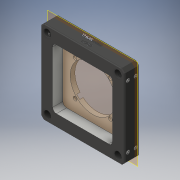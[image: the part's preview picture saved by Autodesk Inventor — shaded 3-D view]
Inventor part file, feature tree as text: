
AUTODESK INVENTOR PART (.ipt)
format: ipt  version: 2016 (Build 200138000, 138)  size: 1,070,592 bytes
history: native  units: in
note: dims shown in document units (in); Inventor stores cm internally (conversion verified against a paired STEP export)
features: other x9, sketch x4, projected_geometry x4, extrude x3, plane x1, hole x1, pattern_circular x1
ambient origin geometry x8: Origin, YZ Plane, XZ Plane, XY Plane, X Axis, Y Axis, Z Axis, Center Point
bodies: Solid1 (feature_tree), Solid2 (feature_tree), Solid3 (feature_tree), Solid4 (feature_tree), Solid5 (feature_tree), Solid6 (feature_tree), Solid7 (feature_tree), Solid8 (feature_tree), Solid9 (feature_tree)
feature tree (23):
  plane  "Work Plane1"
  extrude  "Extrusion5"  Depth=1.0in TaperAngle=0.0deg
  extrude  "Extrusion6"  Depth=2.0in
  extrude  "Extrusion7"  Depth=0.125in TaperAngle=0.0deg
  hole  "Hole2"  [1 undecoded]
  pattern_circular  "Circular Pattern2"  [2 undecoded]
  sketch  "Sketch1"  dims[d5=-0.3425in d10=1.0in d11=0.0in]
  projected_geometry  "Projected Loop1"
  sketch  "Sketch4"  dims[d12=2.0in d13=2.0in]
  projected_geometry  "Projected Loop4"
  sketch  "Sketch5"  dims[d14=0.125in d15=1.0in d16=0.0in]
  projected_geometry  "Projected Loop5"
  sketch  "Sketch6"  dims[d17=1.5129in d18=1.0in d19=0.0in d20=1.6703in d31=0.129in d32=0.224in d33=0.219in d34=0.112in d35=0.5635in d36=0.349in d37=0.8108in d38=1.5748in d39=360.0deg]
  projected_geometry  "Projected Loop6"
  other  "13107-001-1-solid1"
  other  "SS4S019-1-1-solid1"
  other  "SS4S019-1-2-solid1"
  other  "SS4S019-1-3-solid1"
  other  "SS4S019-1-4-solid1"
  other  "SS4S019-1-5-solid1"
  other  "SS4S019-1-6-solid1"
  other  "SS4S019-1-7-solid1"
  other  "SS4S019-1-8-solid1"
note: 3 required parameter values undecoded (feature->parameter linkage not recoverable at this tier; creation-order binding heuristic only, values carry confidence <= 0.55)
